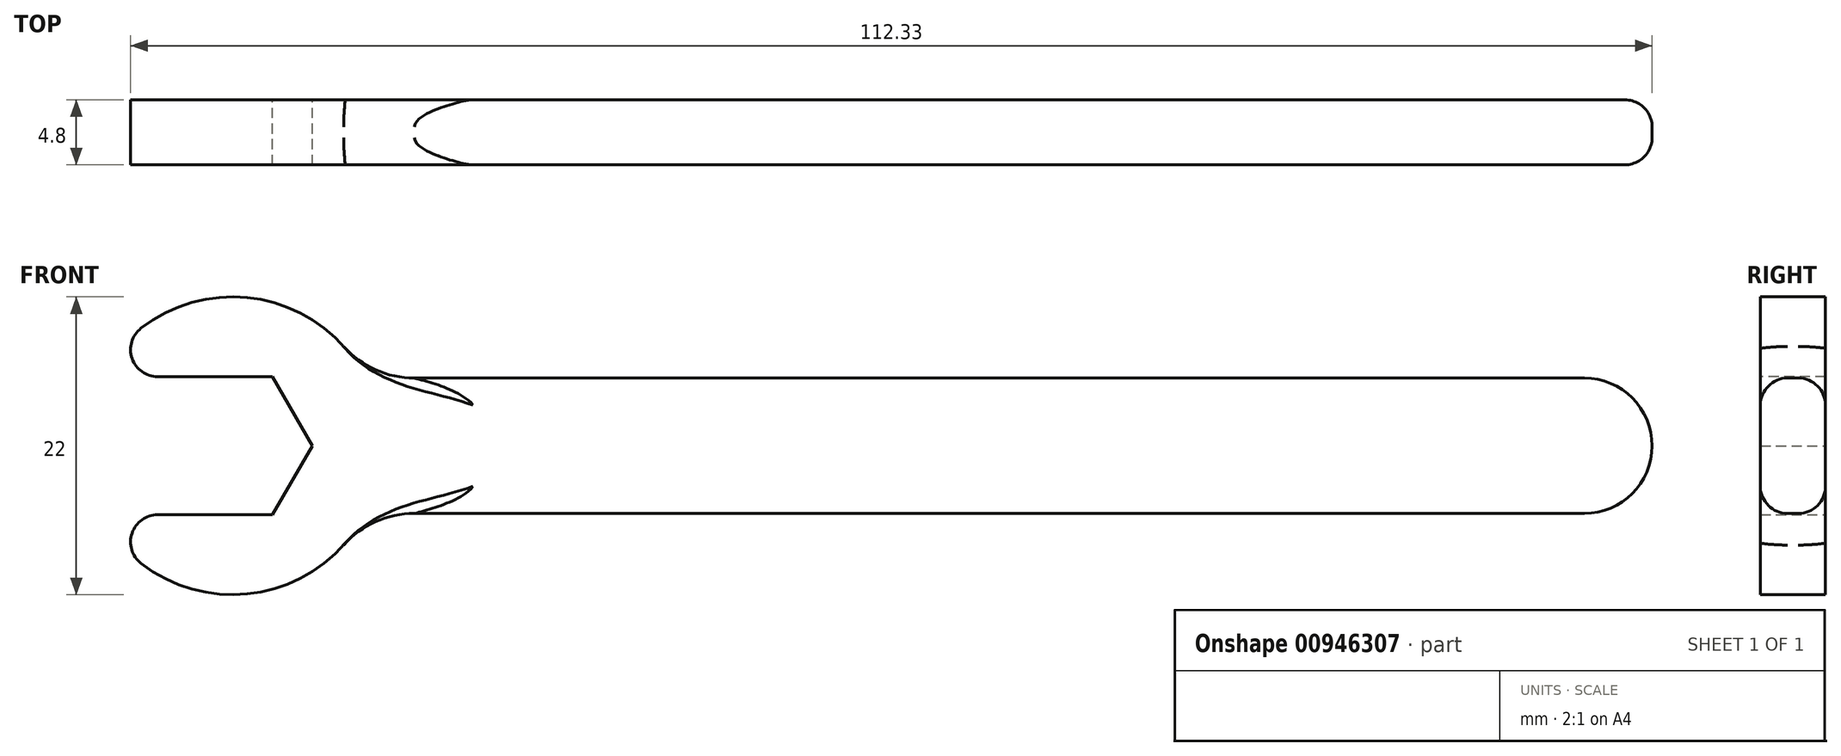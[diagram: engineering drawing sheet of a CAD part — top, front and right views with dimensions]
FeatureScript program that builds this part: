
annotation { "Feature Type Name" : "Feature", "Feature Type Description" : "" }
export const myFeature = defineFeature(function(context is Context, id is Id, definition is map)
    precondition{}
    {
        {
            var Q0;
            Q0=qCreatedBy(makeId("Front.planeOp"),FACE);
            var sketch = newSketch(context, id + "F0", { "sketchPlane" : qUnion([Q0])});
            skCircle(sketch, "E0", {"center": v(0, 0) * mm, "radius": 11 * mm});
            skLineSegment(sketch, "E1", {"start": v(0, 22.1) * mm, "end": v(0, -25.08) * mm, "construction": true});
            skLineSegment(sketch, "E2", {"start": v(-29.72, 0) * mm, "end": v(78.74, 0) * mm, "construction": true});
            skLineSegment(sketch, "E3.bottom", {"start": v(9.8, 5) * mm, "end": v(104.8, 5) * mm});
            skLineSegment(sketch, "E3.top", {"start": v(9.8, -5) * mm, "end": v(104.8, -5) * mm});
            skLineSegment(sketch, "E3.left", {"start": v(9.8, 5) * mm, "end": v(9.8, -5) * mm});
            skLineSegment(sketch, "E3.right", {"start": v(104.8, 5) * mm, "end": v(104.8, -5) * mm});
            skCircle(sketch, "E4.cCircle", {"center": v(0, 0) * mm, "radius": 5.1 * mm, "construction": true});
            skLineSegment(sketch, "E4.0", {"start": v(-2.94, 5.1) * mm, "end": v(2.94, 5.1) * mm});
            skLineSegment(sketch, "E4.1", {"start": v(2.94, 5.1) * mm, "end": v(5.89, 0) * mm});
            skLineSegment(sketch, "E4.2", {"start": v(5.89, 0) * mm, "end": v(2.94, -5.1) * mm});
            skLineSegment(sketch, "E4.3", {"start": v(2.94, -5.1) * mm, "end": v(-2.94, -5.1) * mm});
            skLineSegment(sketch, "E4.4", {"start": v(-2.94, -5.1) * mm, "end": v(-5.89, 0) * mm});
            skLineSegment(sketch, "E4.5", {"start": v(-5.89, 0) * mm, "end": v(-2.94, 5.1) * mm});
            skPoint(sketch, "E4.0.midPoint", {"position": v(0, 5.1) * mm});
            skLineSegment(sketch, "E5", {"start": v(-2.94, 5.1) * mm, "end": v(-9.75, 5.1) * mm});
            skLineSegment(sketch, "E6", {"start": v(-2.94, -5.1) * mm, "end": v(-9.75, -5.1) * mm});
            skSolve(sketch);
        }
        {
            var Q0;
            {var subQ0=sQuery(id+"F0.wireOp",EDGE,"E3.left");Q0=makeQuery(id+"F0.imprint","IMPRINT",FACE,{"disambiguationData":[TD([[makeQuery(id+"F0.imprint","IMPRINT",EDGE,{"derivedFrom":subQ0}),-1.0]])]});}
            var Q1;
            {var subQ1=sQuery(id+"F0.wireOp",EDGE,"E3.bottom");Q1=makeQuery(id+"F0.imprint","IMPRINT",FACE,{"disambiguationData":[TD([[makeQuery(id+"F0.imprint","IMPRINT",EDGE,{"derivedFrom":subQ1}),-1.0]])]});}
            var Q2;
            {var subQ0=sQuery(id+"F0.wireOp",EDGE,"E3.left");Q2=makeQuery(id+"F0.imprint","IMPRINT",FACE,{"disambiguationData":[TD([[makeQuery(id+"F0.imprint","IMPRINT",EDGE,{"derivedFrom":subQ0}),1.0]])]});}
            extrude(context, id + "F1", {"entities" : qUnion([Q0, Q1, Q2]), "depth" : 4.8 * mm, "offsetDistance" : 25 * mm});
        }
        {
            var Q0;
            Q0=makeQuery(id+"F1.opExtrude","SWEPT_EDGE",EDGE,{"disambiguationData":[OSD([sQuery(id+"F0.wireOp",EDGE,"E0"),sQuery(id+"F0.wireOp",EDGE,"E5")])]});
            var Q1;
            Q1=makeQuery(id+"F1.opExtrude","SWEPT_EDGE",EDGE,{"disambiguationData":[OSD([sQuery(id+"F0.wireOp",EDGE,"E0"),sQuery(id+"F0.wireOp",EDGE,"E6")])]});
            fillet(context, id + "F2", {"entities" : qUnion([Q0, Q1]), "radius" : 2 * mm, "tangentPropagation" : true, "allowEdgeOverflow" : false});
        }
        {
            var Q0;
            Q0=makeQuery(id+"F1.opExtrude","SWEPT_EDGE",EDGE,{"disambiguationData":[OSD([sQuery(id+"F0.wireOp",EDGE,"E3.bottom"),sQuery(id+"F0.wireOp",EDGE,"E3.right")])]});
            var Q1;
            Q1=makeQuery(id+"F1.opExtrude","SWEPT_EDGE",EDGE,{"disambiguationData":[OSD([sQuery(id+"F0.wireOp",EDGE,"E3.top"),sQuery(id+"F0.wireOp",EDGE,"E3.right")])]});
            fillet(context, id + "F3", {"entities" : qUnion([Q0, Q1]), "radius" : 5 * mm, "tangentPropagation" : true, "allowEdgeOverflow" : false});
        }
        {
            var Q0;
            Q0=makeQuery(id+"F1.opExtrude","CAP_EDGE",EDGE,{"disambiguationData":[OSD([sQuery(id+"F0.wireOp",EDGE,"E3.bottom")])],"isStart":false});
            var Q1;
            Q1=makeQuery(id+"F1.opExtrude","CAP_EDGE",EDGE,{"disambiguationData":[OSD([sQuery(id+"F0.wireOp",EDGE,"E3.bottom")])],"isStart":true});
            fillet(context, id + "F4", {"entities" : qUnion([Q0, Q1]), "radius" : 2 * mm, "tangentPropagation" : true, "allowEdgeOverflow" : false});
        }
        {
            var Q0;
            Q0=makeQuery(id+"F1.opExtrude","SWEPT_EDGE",EDGE,{"disambiguationData":[OSD([sQuery(id+"F0.wireOp",EDGE,"E0"),sQuery(id+"F0.wireOp",EDGE,"E3.bottom"),sQuery(id+"F0.wireOp",EDGE,"E3.left")])]});
            var Q1;
            Q1=makeQuery(id+"F1.opExtrude","SWEPT_EDGE",EDGE,{"disambiguationData":[OSD([sQuery(id+"F0.wireOp",EDGE,"E0"),sQuery(id+"F0.wireOp",EDGE,"E3.top"),sQuery(id+"F0.wireOp",EDGE,"E3.left")])]});
            fillet(context, id + "F5", {"entities" : qUnion([Q0, Q1]), "radius" : 7 * mm, "tangentPropagation" : true, "allowEdgeOverflow" : false});
        }
    });
